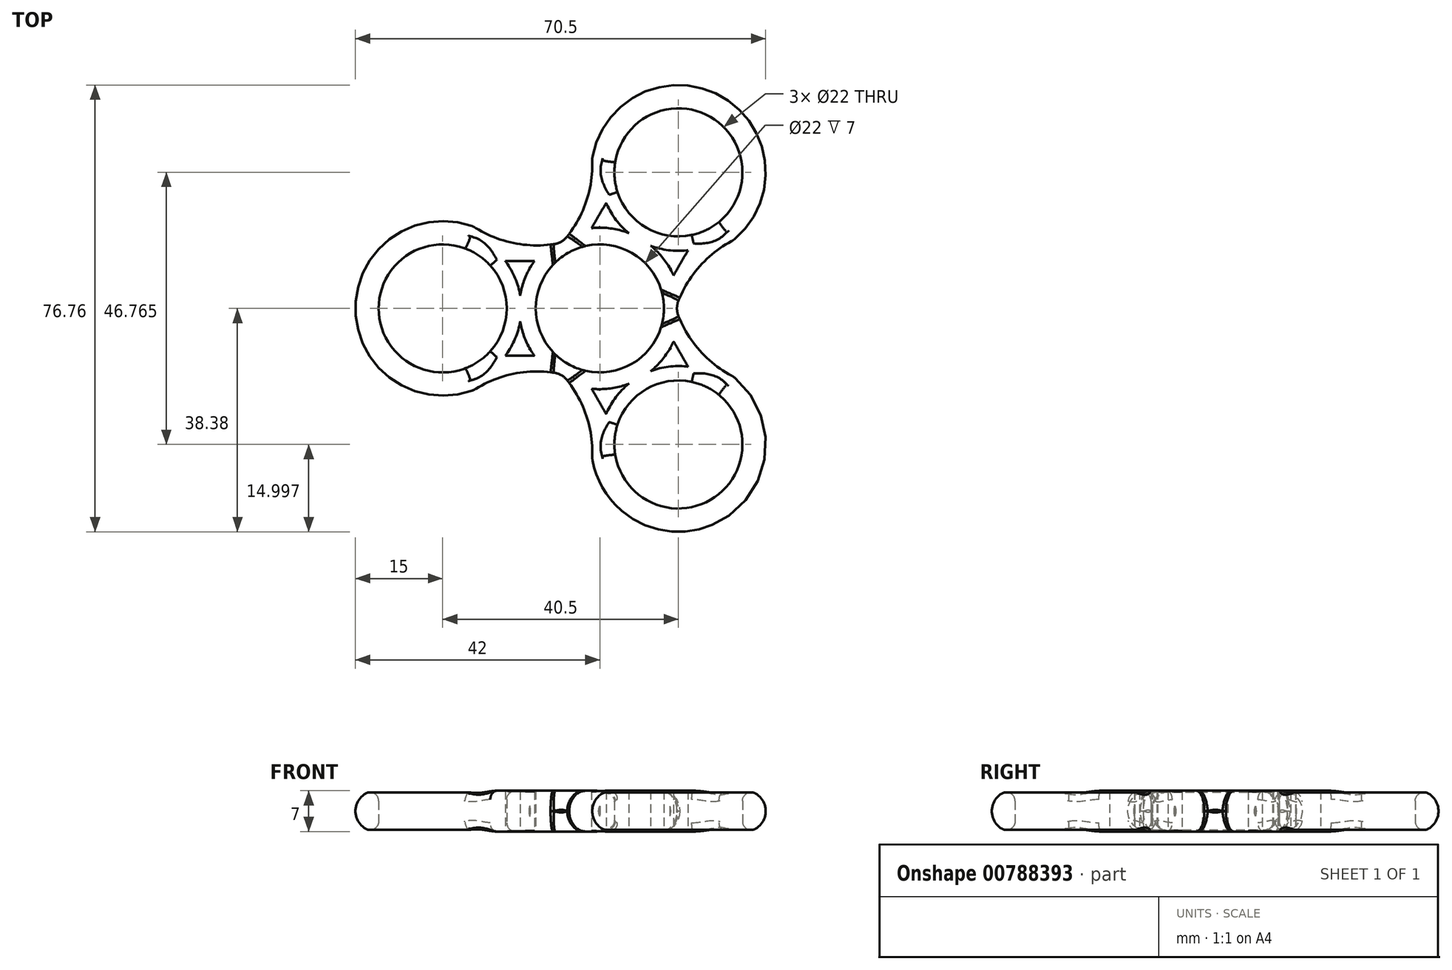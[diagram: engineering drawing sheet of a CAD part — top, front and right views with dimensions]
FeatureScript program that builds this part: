
annotation { "Feature Type Name" : "Feature", "Feature Type Description" : "" }
export const myFeature = defineFeature(function(context is Context, id is Id, definition is map)
    precondition{}
    {
        {
            var Q0;
            Q0=qCreatedBy(makeId("Front.planeOp"),FACE);
            var sketch = newSketch(context, id + "F0", { "sketchPlane" : qUnion([Q0])});
            skLineSegment(sketch, "E0", {"start": v(0, 0) * mm, "end": v(0, 6.18) * mm});
            skSolve(sketch);
        }
        {
            var Q0;
            Q0=qCreatedBy(makeId("Top.planeOp"),FACE);
            var sketch = newSketch(context, id + "F1", { "sketchPlane" : qUnion([Q0])});
            skArc(sketch, "E1", {"start": v(0, 11) * mm, "mid": v(-11, 0) * mm, "end": v(0, -11) * mm});
            skLineSegment(sketch, "E2", {"start": v(0, 56.07) * mm, "end": v(0, 11) * mm, "construction": true});
            skLineSegment(sketch, "E3", {"start": v(-42, 56.32) * mm, "end": v(-42, -55.95) * mm, "construction": true});
            skArc(sketch, "E4", {"start": v(-21.61, 14) * mm, "mid": v(-42, 0) * mm, "end": v(-21.61, -14) * mm});
            skLineSegment(sketch, "E5", {"start": v(0, 14) * mm, "end": v(0, 11) * mm});
            skLineSegment(sketch, "E6.trimOffspring", {"start": v(0, -11) * mm, "end": v(0, -55.82) * mm, "construction": true});
            skLineSegment(sketch, "E7.trimOffspring", {"start": v(0, -11) * mm, "end": v(0, -14) * mm});
            skCircle(sketch, "E8", {"center": v(-27, 0) * mm, "radius": 11 * mm});
            skArc(sketch, "E9", {"start": v(-21.61, 14) * mm, "mid": v(-10.8, 10.83) * mm, "end": v(0, 14) * mm});
            skArc(sketch, "E10", {"start": v(0, -14) * mm, "mid": v(-10.8, -10.83) * mm, "end": v(-21.61, -14) * mm});
            skArc(sketch, "E11", {"start": v(-16.24, -8.13) * mm, "mid": v(-14.6, -5.32) * mm, "end": v(-13.7, -2.2) * mm});
            skArc(sketch, "E12", {"start": v(-13.7, -2.2) * mm, "mid": v(-12.82, -5.3) * mm, "end": v(-11.24, -8.13) * mm});
            skLineSegment(sketch, "E13", {"start": v(-16.24, 8.13) * mm, "end": v(-11.24, 8.13) * mm});
            skLineSegment(sketch, "E14", {"start": v(-16.24, -8.13) * mm, "end": v(-11.24, -8.13) * mm});
            skArc(sketch, "E15.trimOffspring", {"start": v(-13.7, 2.2) * mm, "mid": v(-14.6, 5.32) * mm, "end": v(-16.24, 8.13) * mm});
            skArc(sketch, "E16.trimOffspring", {"start": v(-11.24, 8.13) * mm, "mid": v(-12.82, 5.3) * mm, "end": v(-13.7, 2.2) * mm});
            skArc(sketch, "E17.trimOffspring", {"start": v(0, 13.87) * mm, "mid": v(-0.1, 13.87) * mm, "end": v(-0.2, 13.87) * mm});
            skArc(sketch, "E18.trimOffspring", {"start": v(-0.2, -13.87) * mm, "mid": v(-0.1, -13.87) * mm, "end": v(0, -13.87) * mm});
            skSolve(sketch);
        }
        {
            var Q0;
            Q0=qSketchRegion(id+"F1",true);
            extrude(context, id + "F2", {"entities" : qUnion([Q0]), "depth" : 7 * mm, "offsetDistance" : 25 * mm});
        }
        {
            var Q0;
            Q0=makeQuery(id+"F2.opExtrude","SWEPT_BODY",BODY,{"disambiguationData":[OSD([sQuery(id+"F1.wireOp",EDGE,"E1"),sQuery(id+"F1.wireOp",EDGE,"E4"),sQuery(id+"F1.wireOp",EDGE,"FDauGuLe-8Zff-q5YO-oCp6-tykGBjxohg7e"),sQuery(id+"F1.wireOp",EDGE,"jIsLD8pJ-Ysfo-LJuf-yR93-SOJIJmbdSe7O"),sQuery(id+"F1.wireOp",EDGE,"E5"),sQuery(id+"F1.wireOp",EDGE,"E7.trimOffspring"),sQuery(id+"F1.wireOp",EDGE,"E8")])]});
            var Q1;
            Q1=sQuery(id+"F0.wireOp",EDGE,"E0");
            circularPattern(context, id + "F3", {"operationType" : NewBodyOperationType.ADD, "entities" : qUnion([Q0]), "axis" : qUnion([Q1]), "angle" : 240 * degree, "instanceCount" : 3, "equalSpace" : true});
        }
        {
            var Q0;
            Q0=makeQuery(id+"F3.boolean.opBoolean","INTERSECT",EDGE,{"derivedFrom":[makeQuery(id+"F2.opExtrude","SWEPT_FACE",FACE,{"disambiguationData":[OSD([sQuery(id+"F1.wireOp",EDGE,"E10")])]}),makeQuery(id+"F3.opPattern","COPY",FACE,{"derivedFrom":makeQuery(id+"F2.opExtrude","SWEPT_FACE",FACE,{"disambiguationData":[OSD([sQuery(id+"F1.wireOp",EDGE,"E9")])]}),"instanceName":"1"})]});
            var Q1;
            Q1=makeQuery(id+"F2.opExtrude","SWEPT_EDGE",EDGE,{"disambiguationData":[OSD([sQuery(id+"F1.wireOp",EDGE,"E4"),sQuery(id+"F1.wireOp",EDGE,"E10")])]});
            var Q2;
            Q2=makeQuery(id+"F3.opPattern","COPY",EDGE,{"derivedFrom":makeQuery(id+"F2.opExtrude","SWEPT_EDGE",EDGE,{"disambiguationData":[OSD([sQuery(id+"F1.wireOp",EDGE,"E4"),sQuery(id+"F1.wireOp",EDGE,"E9")])]}),"instanceName":"1"});
            var Q3;
            Q3=makeQuery(id+"F3.boolean.opBoolean","INTERSECT",EDGE,{"derivedFrom":[makeQuery(id+"F3.opPattern","COPY",FACE,{"derivedFrom":makeQuery(id+"F2.opExtrude","SWEPT_FACE",FACE,{"disambiguationData":[OSD([sQuery(id+"F1.wireOp",EDGE,"E10")])]}),"instanceName":"1"}),makeQuery(id+"F3.opPattern","COPY",FACE,{"derivedFrom":makeQuery(id+"F2.opExtrude","SWEPT_FACE",FACE,{"disambiguationData":[OSD([sQuery(id+"F1.wireOp",EDGE,"E9")])]}),"instanceName":"2"})]});
            var Q4;
            Q4=makeQuery(id+"F3.opPattern","COPY",EDGE,{"derivedFrom":makeQuery(id+"F2.opExtrude","SWEPT_EDGE",EDGE,{"disambiguationData":[OSD([sQuery(id+"F1.wireOp",EDGE,"E4"),sQuery(id+"F1.wireOp",EDGE,"E10")])]}),"instanceName":"1"});
            var Q5;
            Q5=makeQuery(id+"F3.opPattern","COPY",EDGE,{"derivedFrom":makeQuery(id+"F2.opExtrude","SWEPT_EDGE",EDGE,{"disambiguationData":[OSD([sQuery(id+"F1.wireOp",EDGE,"E4"),sQuery(id+"F1.wireOp",EDGE,"E9")])]}),"instanceName":"2"});
            var Q6;
            Q6=makeQuery(id+"F3.opPattern","COPY",EDGE,{"derivedFrom":makeQuery(id+"F2.opExtrude","SWEPT_EDGE",EDGE,{"disambiguationData":[OSD([sQuery(id+"F1.wireOp",EDGE,"E4"),sQuery(id+"F1.wireOp",EDGE,"E10")])]}),"instanceName":"2"});
            var Q7;
            Q7=makeQuery(id+"F3.boolean.opBoolean","INTERSECT",EDGE,{"derivedFrom":[makeQuery(id+"F2.opExtrude","SWEPT_FACE",FACE,{"disambiguationData":[OSD([sQuery(id+"F1.wireOp",EDGE,"E9")])]}),makeQuery(id+"F3.opPattern","COPY",FACE,{"derivedFrom":makeQuery(id+"F2.opExtrude","SWEPT_FACE",FACE,{"disambiguationData":[OSD([sQuery(id+"F1.wireOp",EDGE,"E10")])]}),"instanceName":"2"})]});
            var Q8;
            Q8=makeQuery(id+"F2.opExtrude","SWEPT_EDGE",EDGE,{"disambiguationData":[OSD([sQuery(id+"F1.wireOp",EDGE,"E4"),sQuery(id+"F1.wireOp",EDGE,"E9")])]});
            fillet(context, id + "F4", {"entities" : qUnion([Q0, Q1, Q2, Q3, Q4, Q5, Q6, Q7, Q8]), "radius" : 3.5 * mm, "tangentPropagation" : true, "allowEdgeOverflow" : false});
        }
        {
            var Q0;
            Q0=makeQuery(id+"F3.opPattern","COPY",EDGE,{"derivedFrom":makeQuery(id+"F2.opExtrude","CAP_EDGE",EDGE,{"disambiguationData":[OSD([sQuery(id+"F1.wireOp",EDGE,"E4")])],"isStart":false}),"instanceName":"2"});
            var Q1;
            Q1=makeQuery(id+"F3.opPattern","COPY",EDGE,{"derivedFrom":makeQuery(id+"F2.opExtrude","CAP_EDGE",EDGE,{"disambiguationData":[OSD([sQuery(id+"F1.wireOp",EDGE,"E10")])],"isStart":false}),"instanceName":"2"});
            var Q2;
            {var subQ0=sQuery(id+"F1.wireOp",EDGE,"E10");var subQ1=sQuery(id+"F1.wireOp",EDGE,"E9");var subQ2=makeQuery(id+"F2.opExtrude","CAP_FACE",FACE,{"disambiguationData":[OSD([sQuery(id+"F1.wireOp",EDGE,"E1"),sQuery(id+"F1.wireOp",EDGE,"E4"),sQuery(id+"F1.wireOp",EDGE,"E5"),sQuery(id+"F1.wireOp",EDGE,"E7.trimOffspring"),sQuery(id+"F1.wireOp",EDGE,"E8"),subQ1,subQ0])],"isStart":false});Q2=makeQuery(id+"F4.opFillet","BLEND_EDGE",EDGE,{"blendedFrom":[makeQuery(id+"F3.boolean.opBoolean","INTERSECT",EDGE,{"derivedFrom":[makeQuery(id+"F2.opExtrude","SWEPT_FACE",FACE,{"disambiguationData":[OSD([subQ1])]}),makeQuery(id+"F3.opPattern","COPY",FACE,{"derivedFrom":makeQuery(id+"F2.opExtrude","SWEPT_FACE",FACE,{"disambiguationData":[OSD([subQ0])]}),"instanceName":"2"})]}),makeQuery(id+"F3.boolean.opBoolean","MERGE",FACE,{"derivedFrom":[subQ2,makeQuery(id+"F3.opPattern","COPY",FACE,{"derivedFrom":subQ2,"instanceName":"1"}),makeQuery(id+"F3.opPattern","COPY",FACE,{"derivedFrom":subQ2,"instanceName":"2"})]})],"blendedInto":[makeQuery(id+"F3.boolean.opBoolean","MERGE",FACE,{"derivedFrom":[subQ2,makeQuery(id+"F3.opPattern","COPY",FACE,{"derivedFrom":subQ2,"instanceName":"1"}),makeQuery(id+"F3.opPattern","COPY",FACE,{"derivedFrom":subQ2,"instanceName":"2"})]})]});}
            var Q3;
            Q3=makeQuery(id+"F2.opExtrude","CAP_EDGE",EDGE,{"disambiguationData":[OSD([sQuery(id+"F1.wireOp",EDGE,"E9")])],"isStart":false});
            var Q4;
            Q4=makeQuery(id+"F2.opExtrude","CAP_EDGE",EDGE,{"disambiguationData":[OSD([sQuery(id+"F1.wireOp",EDGE,"E4")])],"isStart":false});
            var Q5;
            {var subQ0=sQuery(id+"F1.wireOp",EDGE,"E9");var subQ1=sQuery(id+"F1.wireOp",EDGE,"E4");var subQ2=makeQuery(id+"F2.opExtrude","CAP_FACE",FACE,{"disambiguationData":[OSD([sQuery(id+"F1.wireOp",EDGE,"E1"),subQ1,sQuery(id+"F1.wireOp",EDGE,"E5"),sQuery(id+"F1.wireOp",EDGE,"E7.trimOffspring"),sQuery(id+"F1.wireOp",EDGE,"E8"),subQ0,sQuery(id+"F1.wireOp",EDGE,"E10")])],"isStart":false});Q5=makeQuery(id+"F4.opFillet","BLEND_EDGE",EDGE,{"blendedFrom":[makeQuery(id+"F2.opExtrude","SWEPT_EDGE",EDGE,{"disambiguationData":[OSD([subQ1,subQ0])]}),makeQuery(id+"F3.boolean.opBoolean","MERGE",FACE,{"derivedFrom":[subQ2,makeQuery(id+"F3.opPattern","COPY",FACE,{"derivedFrom":subQ2,"instanceName":"1"}),makeQuery(id+"F3.opPattern","COPY",FACE,{"derivedFrom":subQ2,"instanceName":"2"})]})],"blendedInto":[makeQuery(id+"F3.boolean.opBoolean","MERGE",FACE,{"derivedFrom":[subQ2,makeQuery(id+"F3.opPattern","COPY",FACE,{"derivedFrom":subQ2,"instanceName":"1"}),makeQuery(id+"F3.opPattern","COPY",FACE,{"derivedFrom":subQ2,"instanceName":"2"})]})]});}
            var Q6;
            {var subQ0=sQuery(id+"F1.wireOp",EDGE,"E10");var subQ1=sQuery(id+"F1.wireOp",EDGE,"E4");var subQ2=makeQuery(id+"F2.opExtrude","CAP_FACE",FACE,{"disambiguationData":[OSD([sQuery(id+"F1.wireOp",EDGE,"E1"),subQ1,sQuery(id+"F1.wireOp",EDGE,"E5"),sQuery(id+"F1.wireOp",EDGE,"E7.trimOffspring"),sQuery(id+"F1.wireOp",EDGE,"E8"),sQuery(id+"F1.wireOp",EDGE,"E9"),subQ0])],"isStart":false});Q6=makeQuery(id+"F4.opFillet","BLEND_EDGE",EDGE,{"blendedFrom":[makeQuery(id+"F3.opPattern","COPY",EDGE,{"derivedFrom":makeQuery(id+"F2.opExtrude","SWEPT_EDGE",EDGE,{"disambiguationData":[OSD([subQ1,subQ0])]}),"instanceName":"2"}),makeQuery(id+"F3.boolean.opBoolean","MERGE",FACE,{"derivedFrom":[subQ2,makeQuery(id+"F3.opPattern","COPY",FACE,{"derivedFrom":subQ2,"instanceName":"1"}),makeQuery(id+"F3.opPattern","COPY",FACE,{"derivedFrom":subQ2,"instanceName":"2"})]})],"blendedInto":[makeQuery(id+"F3.boolean.opBoolean","MERGE",FACE,{"derivedFrom":[subQ2,makeQuery(id+"F3.opPattern","COPY",FACE,{"derivedFrom":subQ2,"instanceName":"1"}),makeQuery(id+"F3.opPattern","COPY",FACE,{"derivedFrom":subQ2,"instanceName":"2"})]})]});}
            var Q7;
            Q7=makeQuery(id+"F3.opPattern","COPY",EDGE,{"derivedFrom":makeQuery(id+"F2.opExtrude","CAP_EDGE",EDGE,{"disambiguationData":[OSD([sQuery(id+"F1.wireOp",EDGE,"E10")])],"isStart":false}),"instanceName":"1"});
            var Q8;
            {var subQ0=sQuery(id+"F1.wireOp",EDGE,"E10");var subQ1=sQuery(id+"F1.wireOp",EDGE,"E4");var subQ2=makeQuery(id+"F2.opExtrude","CAP_FACE",FACE,{"disambiguationData":[OSD([sQuery(id+"F1.wireOp",EDGE,"E1"),subQ1,sQuery(id+"F1.wireOp",EDGE,"E5"),sQuery(id+"F1.wireOp",EDGE,"E7.trimOffspring"),sQuery(id+"F1.wireOp",EDGE,"E8"),sQuery(id+"F1.wireOp",EDGE,"E9"),subQ0])],"isStart":false});Q8=makeQuery(id+"F4.opFillet","BLEND_EDGE",EDGE,{"blendedFrom":[makeQuery(id+"F3.opPattern","COPY",EDGE,{"derivedFrom":makeQuery(id+"F2.opExtrude","SWEPT_EDGE",EDGE,{"disambiguationData":[OSD([subQ1,subQ0])]}),"instanceName":"1"}),makeQuery(id+"F3.boolean.opBoolean","MERGE",FACE,{"derivedFrom":[subQ2,makeQuery(id+"F3.opPattern","COPY",FACE,{"derivedFrom":subQ2,"instanceName":"1"}),makeQuery(id+"F3.opPattern","COPY",FACE,{"derivedFrom":subQ2,"instanceName":"2"})]})],"blendedInto":[makeQuery(id+"F3.boolean.opBoolean","MERGE",FACE,{"derivedFrom":[subQ2,makeQuery(id+"F3.opPattern","COPY",FACE,{"derivedFrom":subQ2,"instanceName":"1"}),makeQuery(id+"F3.opPattern","COPY",FACE,{"derivedFrom":subQ2,"instanceName":"2"})]})]});}
            var Q9;
            Q9=makeQuery(id+"F3.opPattern","COPY",EDGE,{"derivedFrom":makeQuery(id+"F2.opExtrude","CAP_EDGE",EDGE,{"disambiguationData":[OSD([sQuery(id+"F1.wireOp",EDGE,"E4")])],"isStart":false}),"instanceName":"1"});
            var Q10;
            {var subQ0=sQuery(id+"F1.wireOp",EDGE,"E10");var subQ1=sQuery(id+"F1.wireOp",EDGE,"E9");var subQ2=makeQuery(id+"F2.opExtrude","CAP_FACE",FACE,{"disambiguationData":[OSD([sQuery(id+"F1.wireOp",EDGE,"E1"),sQuery(id+"F1.wireOp",EDGE,"E4"),sQuery(id+"F1.wireOp",EDGE,"E5"),sQuery(id+"F1.wireOp",EDGE,"E7.trimOffspring"),sQuery(id+"F1.wireOp",EDGE,"E8"),subQ1,subQ0])],"isStart":false});Q10=makeQuery(id+"F4.opFillet","BLEND_EDGE",EDGE,{"blendedFrom":[makeQuery(id+"F3.boolean.opBoolean","INTERSECT",EDGE,{"derivedFrom":[makeQuery(id+"F3.opPattern","COPY",FACE,{"derivedFrom":makeQuery(id+"F2.opExtrude","SWEPT_FACE",FACE,{"disambiguationData":[OSD([subQ0])]}),"instanceName":"1"}),makeQuery(id+"F3.opPattern","COPY",FACE,{"derivedFrom":makeQuery(id+"F2.opExtrude","SWEPT_FACE",FACE,{"disambiguationData":[OSD([subQ1])]}),"instanceName":"2"})]}),makeQuery(id+"F3.boolean.opBoolean","MERGE",FACE,{"derivedFrom":[subQ2,makeQuery(id+"F3.opPattern","COPY",FACE,{"derivedFrom":subQ2,"instanceName":"1"}),makeQuery(id+"F3.opPattern","COPY",FACE,{"derivedFrom":subQ2,"instanceName":"2"})]})],"blendedInto":[makeQuery(id+"F3.boolean.opBoolean","MERGE",FACE,{"derivedFrom":[subQ2,makeQuery(id+"F3.opPattern","COPY",FACE,{"derivedFrom":subQ2,"instanceName":"1"}),makeQuery(id+"F3.opPattern","COPY",FACE,{"derivedFrom":subQ2,"instanceName":"2"})]})]});}
            var Q11;
            Q11=makeQuery(id+"F3.opPattern","COPY",EDGE,{"derivedFrom":makeQuery(id+"F2.opExtrude","CAP_EDGE",EDGE,{"disambiguationData":[OSD([sQuery(id+"F1.wireOp",EDGE,"E9")])],"isStart":false}),"instanceName":"2"});
            var Q12;
            {var subQ0=sQuery(id+"F1.wireOp",EDGE,"E9");var subQ1=sQuery(id+"F1.wireOp",EDGE,"E4");var subQ2=makeQuery(id+"F2.opExtrude","CAP_FACE",FACE,{"disambiguationData":[OSD([sQuery(id+"F1.wireOp",EDGE,"E1"),subQ1,sQuery(id+"F1.wireOp",EDGE,"E5"),sQuery(id+"F1.wireOp",EDGE,"E7.trimOffspring"),sQuery(id+"F1.wireOp",EDGE,"E8"),subQ0,sQuery(id+"F1.wireOp",EDGE,"E10")])],"isStart":false});Q12=makeQuery(id+"F4.opFillet","BLEND_EDGE",EDGE,{"blendedFrom":[makeQuery(id+"F3.opPattern","COPY",EDGE,{"derivedFrom":makeQuery(id+"F2.opExtrude","SWEPT_EDGE",EDGE,{"disambiguationData":[OSD([subQ1,subQ0])]}),"instanceName":"2"}),makeQuery(id+"F3.boolean.opBoolean","MERGE",FACE,{"derivedFrom":[subQ2,makeQuery(id+"F3.opPattern","COPY",FACE,{"derivedFrom":subQ2,"instanceName":"1"}),makeQuery(id+"F3.opPattern","COPY",FACE,{"derivedFrom":subQ2,"instanceName":"2"})]})],"blendedInto":[makeQuery(id+"F3.boolean.opBoolean","MERGE",FACE,{"derivedFrom":[subQ2,makeQuery(id+"F3.opPattern","COPY",FACE,{"derivedFrom":subQ2,"instanceName":"1"}),makeQuery(id+"F3.opPattern","COPY",FACE,{"derivedFrom":subQ2,"instanceName":"2"})]})]});}
            var Q13;
            Q13=makeQuery(id+"F3.opPattern","COPY",EDGE,{"derivedFrom":makeQuery(id+"F2.opExtrude","CAP_EDGE",EDGE,{"disambiguationData":[OSD([sQuery(id+"F1.wireOp",EDGE,"E9")])],"isStart":false}),"instanceName":"1"});
            var Q14;
            {var subQ0=sQuery(id+"F1.wireOp",EDGE,"E9");var subQ1=sQuery(id+"F1.wireOp",EDGE,"E4");var subQ2=makeQuery(id+"F2.opExtrude","CAP_FACE",FACE,{"disambiguationData":[OSD([sQuery(id+"F1.wireOp",EDGE,"E1"),subQ1,sQuery(id+"F1.wireOp",EDGE,"E5"),sQuery(id+"F1.wireOp",EDGE,"E7.trimOffspring"),sQuery(id+"F1.wireOp",EDGE,"E8"),subQ0,sQuery(id+"F1.wireOp",EDGE,"E10")])],"isStart":false});Q14=makeQuery(id+"F4.opFillet","BLEND_EDGE",EDGE,{"blendedFrom":[makeQuery(id+"F3.opPattern","COPY",EDGE,{"derivedFrom":makeQuery(id+"F2.opExtrude","SWEPT_EDGE",EDGE,{"disambiguationData":[OSD([subQ1,subQ0])]}),"instanceName":"1"}),makeQuery(id+"F3.boolean.opBoolean","MERGE",FACE,{"derivedFrom":[subQ2,makeQuery(id+"F3.opPattern","COPY",FACE,{"derivedFrom":subQ2,"instanceName":"1"}),makeQuery(id+"F3.opPattern","COPY",FACE,{"derivedFrom":subQ2,"instanceName":"2"})]})],"blendedInto":[makeQuery(id+"F3.boolean.opBoolean","MERGE",FACE,{"derivedFrom":[subQ2,makeQuery(id+"F3.opPattern","COPY",FACE,{"derivedFrom":subQ2,"instanceName":"1"}),makeQuery(id+"F3.opPattern","COPY",FACE,{"derivedFrom":subQ2,"instanceName":"2"})]})]});}
            var Q15;
            Q15=makeQuery(id+"F2.opExtrude","CAP_EDGE",EDGE,{"disambiguationData":[OSD([sQuery(id+"F1.wireOp",EDGE,"E10")])],"isStart":false});
            var Q16;
            {var subQ0=sQuery(id+"F1.wireOp",EDGE,"E10");var subQ1=sQuery(id+"F1.wireOp",EDGE,"E4");var subQ2=makeQuery(id+"F2.opExtrude","CAP_FACE",FACE,{"disambiguationData":[OSD([sQuery(id+"F1.wireOp",EDGE,"E1"),subQ1,sQuery(id+"F1.wireOp",EDGE,"E5"),sQuery(id+"F1.wireOp",EDGE,"E7.trimOffspring"),sQuery(id+"F1.wireOp",EDGE,"E8"),sQuery(id+"F1.wireOp",EDGE,"E9"),subQ0])],"isStart":false});Q16=makeQuery(id+"F4.opFillet","BLEND_EDGE",EDGE,{"blendedFrom":[makeQuery(id+"F2.opExtrude","SWEPT_EDGE",EDGE,{"disambiguationData":[OSD([subQ1,subQ0])]}),makeQuery(id+"F3.boolean.opBoolean","MERGE",FACE,{"derivedFrom":[subQ2,makeQuery(id+"F3.opPattern","COPY",FACE,{"derivedFrom":subQ2,"instanceName":"1"}),makeQuery(id+"F3.opPattern","COPY",FACE,{"derivedFrom":subQ2,"instanceName":"2"})]})],"blendedInto":[makeQuery(id+"F3.boolean.opBoolean","MERGE",FACE,{"derivedFrom":[subQ2,makeQuery(id+"F3.opPattern","COPY",FACE,{"derivedFrom":subQ2,"instanceName":"1"}),makeQuery(id+"F3.opPattern","COPY",FACE,{"derivedFrom":subQ2,"instanceName":"2"})]})]});}
            var Q17;
            {var subQ0=sQuery(id+"F1.wireOp",EDGE,"E10");var subQ1=sQuery(id+"F1.wireOp",EDGE,"E9");var subQ2=makeQuery(id+"F2.opExtrude","CAP_FACE",FACE,{"disambiguationData":[OSD([sQuery(id+"F1.wireOp",EDGE,"E1"),sQuery(id+"F1.wireOp",EDGE,"E4"),sQuery(id+"F1.wireOp",EDGE,"E5"),sQuery(id+"F1.wireOp",EDGE,"E7.trimOffspring"),sQuery(id+"F1.wireOp",EDGE,"E8"),subQ1,subQ0])],"isStart":false});Q17=makeQuery(id+"F4.opFillet","BLEND_EDGE",EDGE,{"blendedFrom":[makeQuery(id+"F3.boolean.opBoolean","INTERSECT",EDGE,{"derivedFrom":[makeQuery(id+"F2.opExtrude","SWEPT_FACE",FACE,{"disambiguationData":[OSD([subQ0])]}),makeQuery(id+"F3.opPattern","COPY",FACE,{"derivedFrom":makeQuery(id+"F2.opExtrude","SWEPT_FACE",FACE,{"disambiguationData":[OSD([subQ1])]}),"instanceName":"1"})]}),makeQuery(id+"F3.boolean.opBoolean","MERGE",FACE,{"derivedFrom":[subQ2,makeQuery(id+"F3.opPattern","COPY",FACE,{"derivedFrom":subQ2,"instanceName":"1"}),makeQuery(id+"F3.opPattern","COPY",FACE,{"derivedFrom":subQ2,"instanceName":"2"})]})],"blendedInto":[makeQuery(id+"F3.boolean.opBoolean","MERGE",FACE,{"derivedFrom":[subQ2,makeQuery(id+"F3.opPattern","COPY",FACE,{"derivedFrom":subQ2,"instanceName":"1"}),makeQuery(id+"F3.opPattern","COPY",FACE,{"derivedFrom":subQ2,"instanceName":"2"})]})]});}
            fillet(context, id + "F5", {"entities" : qUnion([Q0, Q1, Q2, Q3, Q4, Q5, Q6, Q7, Q8, Q9, Q10, Q11, Q12, Q13, Q14, Q15, Q16, Q17]), "radius" : 3.5 * mm, "tangentPropagation" : true, "allowEdgeOverflow" : false});
        }
        {
            var Q0;
            Q0=makeQuery(id+"F3.opPattern","COPY",EDGE,{"derivedFrom":makeQuery(id+"F2.opExtrude","CAP_EDGE",EDGE,{"disambiguationData":[OSD([sQuery(id+"F1.wireOp",EDGE,"E4")])],"isStart":true}),"instanceName":"1"});
            var Q1;
            Q1=makeQuery(id+"F3.opPattern","COPY",EDGE,{"derivedFrom":makeQuery(id+"F2.opExtrude","CAP_EDGE",EDGE,{"disambiguationData":[OSD([sQuery(id+"F1.wireOp",EDGE,"E4")])],"isStart":true}),"instanceName":"2"});
            var Q2;
            Q2=makeQuery(id+"F2.opExtrude","CAP_EDGE",EDGE,{"disambiguationData":[OSD([sQuery(id+"F1.wireOp",EDGE,"E4")])],"isStart":true});
            var Q3;
            Q3=makeQuery(id+"F2.opExtrude","CAP_EDGE",EDGE,{"disambiguationData":[OSD([sQuery(id+"F1.wireOp",EDGE,"E10")])],"isStart":true});
            var Q4;
            Q4=makeQuery(id+"F3.opPattern","COPY",EDGE,{"derivedFrom":makeQuery(id+"F2.opExtrude","CAP_EDGE",EDGE,{"disambiguationData":[OSD([sQuery(id+"F1.wireOp",EDGE,"E9")])],"isStart":true}),"instanceName":"1"});
            var Q5;
            Q5=makeQuery(id+"F3.opPattern","COPY",EDGE,{"derivedFrom":makeQuery(id+"F2.opExtrude","CAP_EDGE",EDGE,{"disambiguationData":[OSD([sQuery(id+"F1.wireOp",EDGE,"E10")])],"isStart":true}),"instanceName":"1"});
            var Q6;
            Q6=makeQuery(id+"F3.opPattern","COPY",EDGE,{"derivedFrom":makeQuery(id+"F2.opExtrude","CAP_EDGE",EDGE,{"disambiguationData":[OSD([sQuery(id+"F1.wireOp",EDGE,"E10")])],"isStart":true}),"instanceName":"2"});
            var Q7;
            Q7=makeQuery(id+"F2.opExtrude","CAP_EDGE",EDGE,{"disambiguationData":[OSD([sQuery(id+"F1.wireOp",EDGE,"E9")])],"isStart":true});
            var Q8;
            {var subQ0=sQuery(id+"F1.wireOp",EDGE,"E10");var subQ1=sQuery(id+"F1.wireOp",EDGE,"E9");var subQ2=makeQuery(id+"F2.opExtrude","CAP_FACE",FACE,{"disambiguationData":[OSD([sQuery(id+"F1.wireOp",EDGE,"E1"),sQuery(id+"F1.wireOp",EDGE,"E4"),sQuery(id+"F1.wireOp",EDGE,"E5"),sQuery(id+"F1.wireOp",EDGE,"E7.trimOffspring"),sQuery(id+"F1.wireOp",EDGE,"E8"),subQ1,subQ0])],"isStart":true});Q8=makeQuery(id+"F4.opFillet","BLEND_EDGE",EDGE,{"blendedFrom":[makeQuery(id+"F3.boolean.opBoolean","INTERSECT",EDGE,{"derivedFrom":[makeQuery(id+"F2.opExtrude","SWEPT_FACE",FACE,{"disambiguationData":[OSD([subQ1])]}),makeQuery(id+"F3.opPattern","COPY",FACE,{"derivedFrom":makeQuery(id+"F2.opExtrude","SWEPT_FACE",FACE,{"disambiguationData":[OSD([subQ0])]}),"instanceName":"2"})]}),makeQuery(id+"F3.boolean.opBoolean","MERGE",FACE,{"derivedFrom":[subQ2,makeQuery(id+"F3.opPattern","COPY",FACE,{"derivedFrom":subQ2,"instanceName":"1"}),makeQuery(id+"F3.opPattern","COPY",FACE,{"derivedFrom":subQ2,"instanceName":"2"})]})],"blendedInto":[makeQuery(id+"F3.boolean.opBoolean","MERGE",FACE,{"derivedFrom":[subQ2,makeQuery(id+"F3.opPattern","COPY",FACE,{"derivedFrom":subQ2,"instanceName":"1"}),makeQuery(id+"F3.opPattern","COPY",FACE,{"derivedFrom":subQ2,"instanceName":"2"})]})]});}
            var Q9;
            {var subQ0=sQuery(id+"F1.wireOp",EDGE,"E10");var subQ1=sQuery(id+"F1.wireOp",EDGE,"E9");var subQ2=makeQuery(id+"F2.opExtrude","CAP_FACE",FACE,{"disambiguationData":[OSD([sQuery(id+"F1.wireOp",EDGE,"E1"),sQuery(id+"F1.wireOp",EDGE,"E4"),sQuery(id+"F1.wireOp",EDGE,"E5"),sQuery(id+"F1.wireOp",EDGE,"E7.trimOffspring"),sQuery(id+"F1.wireOp",EDGE,"E8"),subQ1,subQ0])],"isStart":true});Q9=makeQuery(id+"F4.opFillet","BLEND_EDGE",EDGE,{"blendedFrom":[makeQuery(id+"F3.boolean.opBoolean","INTERSECT",EDGE,{"derivedFrom":[makeQuery(id+"F2.opExtrude","SWEPT_FACE",FACE,{"disambiguationData":[OSD([subQ0])]}),makeQuery(id+"F3.opPattern","COPY",FACE,{"derivedFrom":makeQuery(id+"F2.opExtrude","SWEPT_FACE",FACE,{"disambiguationData":[OSD([subQ1])]}),"instanceName":"1"})]}),makeQuery(id+"F3.boolean.opBoolean","MERGE",FACE,{"derivedFrom":[subQ2,makeQuery(id+"F3.opPattern","COPY",FACE,{"derivedFrom":subQ2,"instanceName":"1"}),makeQuery(id+"F3.opPattern","COPY",FACE,{"derivedFrom":subQ2,"instanceName":"2"})]})],"blendedInto":[makeQuery(id+"F3.boolean.opBoolean","MERGE",FACE,{"derivedFrom":[subQ2,makeQuery(id+"F3.opPattern","COPY",FACE,{"derivedFrom":subQ2,"instanceName":"1"}),makeQuery(id+"F3.opPattern","COPY",FACE,{"derivedFrom":subQ2,"instanceName":"2"})]})]});}
            var Q10;
            {var subQ0=sQuery(id+"F1.wireOp",EDGE,"E10");var subQ1=sQuery(id+"F1.wireOp",EDGE,"E4");var subQ2=makeQuery(id+"F2.opExtrude","CAP_FACE",FACE,{"disambiguationData":[OSD([sQuery(id+"F1.wireOp",EDGE,"E1"),subQ1,sQuery(id+"F1.wireOp",EDGE,"E5"),sQuery(id+"F1.wireOp",EDGE,"E7.trimOffspring"),sQuery(id+"F1.wireOp",EDGE,"E8"),sQuery(id+"F1.wireOp",EDGE,"E9"),subQ0])],"isStart":true});Q10=makeQuery(id+"F4.opFillet","BLEND_EDGE",EDGE,{"blendedFrom":[makeQuery(id+"F2.opExtrude","SWEPT_EDGE",EDGE,{"disambiguationData":[OSD([subQ1,subQ0])]}),makeQuery(id+"F3.boolean.opBoolean","MERGE",FACE,{"derivedFrom":[subQ2,makeQuery(id+"F3.opPattern","COPY",FACE,{"derivedFrom":subQ2,"instanceName":"1"}),makeQuery(id+"F3.opPattern","COPY",FACE,{"derivedFrom":subQ2,"instanceName":"2"})]})],"blendedInto":[makeQuery(id+"F3.boolean.opBoolean","MERGE",FACE,{"derivedFrom":[subQ2,makeQuery(id+"F3.opPattern","COPY",FACE,{"derivedFrom":subQ2,"instanceName":"1"}),makeQuery(id+"F3.opPattern","COPY",FACE,{"derivedFrom":subQ2,"instanceName":"2"})]})]});}
            var Q11;
            {var subQ0=sQuery(id+"F1.wireOp",EDGE,"E9");var subQ1=sQuery(id+"F1.wireOp",EDGE,"E4");var subQ2=makeQuery(id+"F2.opExtrude","CAP_FACE",FACE,{"disambiguationData":[OSD([sQuery(id+"F1.wireOp",EDGE,"E1"),subQ1,sQuery(id+"F1.wireOp",EDGE,"E5"),sQuery(id+"F1.wireOp",EDGE,"E7.trimOffspring"),sQuery(id+"F1.wireOp",EDGE,"E8"),subQ0,sQuery(id+"F1.wireOp",EDGE,"E10")])],"isStart":true});Q11=makeQuery(id+"F4.opFillet","BLEND_EDGE",EDGE,{"blendedFrom":[makeQuery(id+"F2.opExtrude","SWEPT_EDGE",EDGE,{"disambiguationData":[OSD([subQ1,subQ0])]}),makeQuery(id+"F3.boolean.opBoolean","MERGE",FACE,{"derivedFrom":[subQ2,makeQuery(id+"F3.opPattern","COPY",FACE,{"derivedFrom":subQ2,"instanceName":"1"}),makeQuery(id+"F3.opPattern","COPY",FACE,{"derivedFrom":subQ2,"instanceName":"2"})]})],"blendedInto":[makeQuery(id+"F3.boolean.opBoolean","MERGE",FACE,{"derivedFrom":[subQ2,makeQuery(id+"F3.opPattern","COPY",FACE,{"derivedFrom":subQ2,"instanceName":"1"}),makeQuery(id+"F3.opPattern","COPY",FACE,{"derivedFrom":subQ2,"instanceName":"2"})]})]});}
            var Q12;
            {var subQ0=sQuery(id+"F1.wireOp",EDGE,"E10");var subQ1=sQuery(id+"F1.wireOp",EDGE,"E4");var subQ2=makeQuery(id+"F2.opExtrude","CAP_FACE",FACE,{"disambiguationData":[OSD([sQuery(id+"F1.wireOp",EDGE,"E1"),subQ1,sQuery(id+"F1.wireOp",EDGE,"E5"),sQuery(id+"F1.wireOp",EDGE,"E7.trimOffspring"),sQuery(id+"F1.wireOp",EDGE,"E8"),sQuery(id+"F1.wireOp",EDGE,"E9"),subQ0])],"isStart":true});Q12=makeQuery(id+"F4.opFillet","BLEND_EDGE",EDGE,{"blendedFrom":[makeQuery(id+"F3.opPattern","COPY",EDGE,{"derivedFrom":makeQuery(id+"F2.opExtrude","SWEPT_EDGE",EDGE,{"disambiguationData":[OSD([subQ1,subQ0])]}),"instanceName":"2"}),makeQuery(id+"F3.boolean.opBoolean","MERGE",FACE,{"derivedFrom":[subQ2,makeQuery(id+"F3.opPattern","COPY",FACE,{"derivedFrom":subQ2,"instanceName":"1"}),makeQuery(id+"F3.opPattern","COPY",FACE,{"derivedFrom":subQ2,"instanceName":"2"})]})],"blendedInto":[makeQuery(id+"F3.boolean.opBoolean","MERGE",FACE,{"derivedFrom":[subQ2,makeQuery(id+"F3.opPattern","COPY",FACE,{"derivedFrom":subQ2,"instanceName":"1"}),makeQuery(id+"F3.opPattern","COPY",FACE,{"derivedFrom":subQ2,"instanceName":"2"})]})]});}
            var Q13;
            Q13=makeQuery(id+"F3.opPattern","COPY",EDGE,{"derivedFrom":makeQuery(id+"F2.opExtrude","CAP_EDGE",EDGE,{"disambiguationData":[OSD([sQuery(id+"F1.wireOp",EDGE,"E9")])],"isStart":true}),"instanceName":"2"});
            var Q14;
            {var subQ0=sQuery(id+"F1.wireOp",EDGE,"E9");var subQ1=sQuery(id+"F1.wireOp",EDGE,"E4");var subQ2=makeQuery(id+"F2.opExtrude","CAP_FACE",FACE,{"disambiguationData":[OSD([sQuery(id+"F1.wireOp",EDGE,"E1"),subQ1,sQuery(id+"F1.wireOp",EDGE,"E5"),sQuery(id+"F1.wireOp",EDGE,"E7.trimOffspring"),sQuery(id+"F1.wireOp",EDGE,"E8"),subQ0,sQuery(id+"F1.wireOp",EDGE,"E10")])],"isStart":true});Q14=makeQuery(id+"F4.opFillet","BLEND_EDGE",EDGE,{"blendedFrom":[makeQuery(id+"F3.opPattern","COPY",EDGE,{"derivedFrom":makeQuery(id+"F2.opExtrude","SWEPT_EDGE",EDGE,{"disambiguationData":[OSD([subQ1,subQ0])]}),"instanceName":"2"}),makeQuery(id+"F3.boolean.opBoolean","MERGE",FACE,{"derivedFrom":[subQ2,makeQuery(id+"F3.opPattern","COPY",FACE,{"derivedFrom":subQ2,"instanceName":"1"}),makeQuery(id+"F3.opPattern","COPY",FACE,{"derivedFrom":subQ2,"instanceName":"2"})]})],"blendedInto":[makeQuery(id+"F3.boolean.opBoolean","MERGE",FACE,{"derivedFrom":[subQ2,makeQuery(id+"F3.opPattern","COPY",FACE,{"derivedFrom":subQ2,"instanceName":"1"}),makeQuery(id+"F3.opPattern","COPY",FACE,{"derivedFrom":subQ2,"instanceName":"2"})]})]});}
            var Q15;
            {var subQ0=sQuery(id+"F1.wireOp",EDGE,"E10");var subQ1=sQuery(id+"F1.wireOp",EDGE,"E9");var subQ2=makeQuery(id+"F2.opExtrude","CAP_FACE",FACE,{"disambiguationData":[OSD([sQuery(id+"F1.wireOp",EDGE,"E1"),sQuery(id+"F1.wireOp",EDGE,"E4"),sQuery(id+"F1.wireOp",EDGE,"E5"),sQuery(id+"F1.wireOp",EDGE,"E7.trimOffspring"),sQuery(id+"F1.wireOp",EDGE,"E8"),subQ1,subQ0])],"isStart":true});Q15=makeQuery(id+"F4.opFillet","BLEND_EDGE",EDGE,{"blendedFrom":[makeQuery(id+"F3.boolean.opBoolean","INTERSECT",EDGE,{"derivedFrom":[makeQuery(id+"F3.opPattern","COPY",FACE,{"derivedFrom":makeQuery(id+"F2.opExtrude","SWEPT_FACE",FACE,{"disambiguationData":[OSD([subQ0])]}),"instanceName":"1"}),makeQuery(id+"F3.opPattern","COPY",FACE,{"derivedFrom":makeQuery(id+"F2.opExtrude","SWEPT_FACE",FACE,{"disambiguationData":[OSD([subQ1])]}),"instanceName":"2"})]}),makeQuery(id+"F3.boolean.opBoolean","MERGE",FACE,{"derivedFrom":[subQ2,makeQuery(id+"F3.opPattern","COPY",FACE,{"derivedFrom":subQ2,"instanceName":"1"}),makeQuery(id+"F3.opPattern","COPY",FACE,{"derivedFrom":subQ2,"instanceName":"2"})]})],"blendedInto":[makeQuery(id+"F3.boolean.opBoolean","MERGE",FACE,{"derivedFrom":[subQ2,makeQuery(id+"F3.opPattern","COPY",FACE,{"derivedFrom":subQ2,"instanceName":"1"}),makeQuery(id+"F3.opPattern","COPY",FACE,{"derivedFrom":subQ2,"instanceName":"2"})]})]});}
            var Q16;
            {var subQ0=sQuery(id+"F1.wireOp",EDGE,"E10");var subQ1=sQuery(id+"F1.wireOp",EDGE,"E4");var subQ2=makeQuery(id+"F2.opExtrude","CAP_FACE",FACE,{"disambiguationData":[OSD([sQuery(id+"F1.wireOp",EDGE,"E1"),subQ1,sQuery(id+"F1.wireOp",EDGE,"E5"),sQuery(id+"F1.wireOp",EDGE,"E7.trimOffspring"),sQuery(id+"F1.wireOp",EDGE,"E8"),sQuery(id+"F1.wireOp",EDGE,"E9"),subQ0])],"isStart":true});Q16=makeQuery(id+"F4.opFillet","BLEND_EDGE",EDGE,{"blendedFrom":[makeQuery(id+"F3.opPattern","COPY",EDGE,{"derivedFrom":makeQuery(id+"F2.opExtrude","SWEPT_EDGE",EDGE,{"disambiguationData":[OSD([subQ1,subQ0])]}),"instanceName":"1"}),makeQuery(id+"F3.boolean.opBoolean","MERGE",FACE,{"derivedFrom":[subQ2,makeQuery(id+"F3.opPattern","COPY",FACE,{"derivedFrom":subQ2,"instanceName":"1"}),makeQuery(id+"F3.opPattern","COPY",FACE,{"derivedFrom":subQ2,"instanceName":"2"})]})],"blendedInto":[makeQuery(id+"F3.boolean.opBoolean","MERGE",FACE,{"derivedFrom":[subQ2,makeQuery(id+"F3.opPattern","COPY",FACE,{"derivedFrom":subQ2,"instanceName":"1"}),makeQuery(id+"F3.opPattern","COPY",FACE,{"derivedFrom":subQ2,"instanceName":"2"})]})]});}
            var Q17;
            {var subQ0=sQuery(id+"F1.wireOp",EDGE,"E9");var subQ1=sQuery(id+"F1.wireOp",EDGE,"E4");var subQ2=makeQuery(id+"F2.opExtrude","CAP_FACE",FACE,{"disambiguationData":[OSD([sQuery(id+"F1.wireOp",EDGE,"E1"),subQ1,sQuery(id+"F1.wireOp",EDGE,"E5"),sQuery(id+"F1.wireOp",EDGE,"E7.trimOffspring"),sQuery(id+"F1.wireOp",EDGE,"E8"),subQ0,sQuery(id+"F1.wireOp",EDGE,"E10")])],"isStart":true});Q17=makeQuery(id+"F4.opFillet","BLEND_EDGE",EDGE,{"blendedFrom":[makeQuery(id+"F3.opPattern","COPY",EDGE,{"derivedFrom":makeQuery(id+"F2.opExtrude","SWEPT_EDGE",EDGE,{"disambiguationData":[OSD([subQ1,subQ0])]}),"instanceName":"1"}),makeQuery(id+"F3.boolean.opBoolean","MERGE",FACE,{"derivedFrom":[subQ2,makeQuery(id+"F3.opPattern","COPY",FACE,{"derivedFrom":subQ2,"instanceName":"1"}),makeQuery(id+"F3.opPattern","COPY",FACE,{"derivedFrom":subQ2,"instanceName":"2"})]})],"blendedInto":[makeQuery(id+"F3.boolean.opBoolean","MERGE",FACE,{"derivedFrom":[subQ2,makeQuery(id+"F3.opPattern","COPY",FACE,{"derivedFrom":subQ2,"instanceName":"1"}),makeQuery(id+"F3.opPattern","COPY",FACE,{"derivedFrom":subQ2,"instanceName":"2"})]})]});}
            fillet(context, id + "F6", {"entities" : qUnion([Q0, Q1, Q2, Q3, Q4, Q5, Q6, Q7, Q8, Q9, Q10, Q11, Q12, Q13, Q14, Q15, Q16, Q17]), "radius" : 3.5 * mm, "tangentPropagation" : true, "allowEdgeOverflow" : false});
        }
        {
            var Q0;
            Q0=makeQuery(id+"F2.opExtrude","CAP_EDGE",EDGE,{"disambiguationData":[OSD([sQuery(id+"F1.wireOp",EDGE,"E8")])],"isStart":false});
            var Q1;
            Q1=makeQuery(id+"F2.opExtrude","CAP_EDGE",EDGE,{"disambiguationData":[OSD([sQuery(id+"F1.wireOp",EDGE,"E8")])],"isStart":true});
            fillet(context, id + "F7", {"entities" : qUnion([Q0, Q1]), "radius" : 1.5 * mm, "tangentPropagation" : true, "allowEdgeOverflow" : false});
        }
        {
            var Q0;
            Q0=makeQuery(id+"F3.opPattern","COPY",EDGE,{"derivedFrom":makeQuery(id+"F2.opExtrude","CAP_EDGE",EDGE,{"disambiguationData":[OSD([sQuery(id+"F1.wireOp",EDGE,"E8")])],"isStart":true}),"instanceName":"2"});
            var Q1;
            Q1=makeQuery(id+"F3.opPattern","COPY",EDGE,{"derivedFrom":makeQuery(id+"F2.opExtrude","CAP_EDGE",EDGE,{"disambiguationData":[OSD([sQuery(id+"F1.wireOp",EDGE,"E8")])],"isStart":false}),"instanceName":"2"});
            var Q2;
            Q2=makeQuery(id+"F3.opPattern","COPY",EDGE,{"derivedFrom":makeQuery(id+"F2.opExtrude","CAP_EDGE",EDGE,{"disambiguationData":[OSD([sQuery(id+"F1.wireOp",EDGE,"E8")])],"isStart":false}),"instanceName":"1"});
            var Q3;
            Q3=makeQuery(id+"F3.opPattern","COPY",EDGE,{"derivedFrom":makeQuery(id+"F2.opExtrude","CAP_EDGE",EDGE,{"disambiguationData":[OSD([sQuery(id+"F1.wireOp",EDGE,"E8")])],"isStart":true}),"instanceName":"1"});
            fillet(context, id + "F8", {"entities" : qUnion([Q0, Q1, Q2, Q3]), "radius" : 1.5 * mm, "tangentPropagation" : true, "allowEdgeOverflow" : false});
        }
    });
